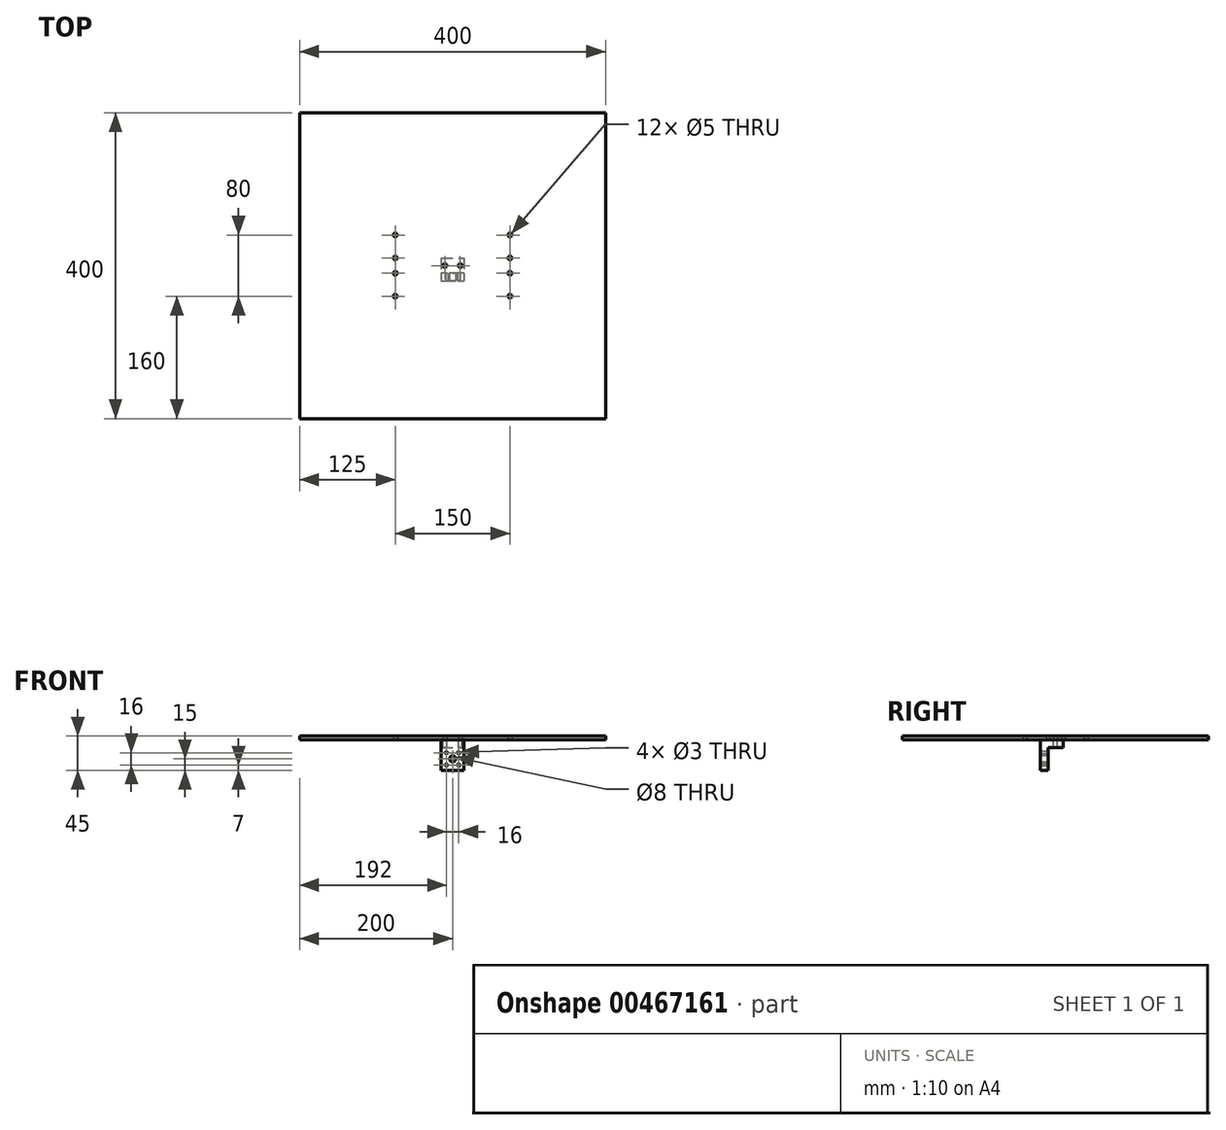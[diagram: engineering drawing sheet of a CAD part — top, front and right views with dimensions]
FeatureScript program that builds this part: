
annotation { "Feature Type Name" : "Feature", "Feature Type Description" : "" }
export const myFeature = defineFeature(function(context is Context, id is Id, definition is map)
    precondition{}
    {
        {
            var Q0;
            Q0=qCreatedBy(makeId("Top.planeOp"),FACE);
            var sketch = newSketch(context, id + "F0", { "sketchPlane" : qUnion([Q0])});
            skLineSegment(sketch, "E0.bottom", {"start": v(-200, 200) * mm, "end": v(200, 200) * mm});
            skLineSegment(sketch, "E0.top", {"start": v(-200, -200) * mm, "end": v(200, -200) * mm});
            skLineSegment(sketch, "E0.left", {"start": v(-200, 200) * mm, "end": v(-200, -200) * mm});
            skLineSegment(sketch, "E0.right", {"start": v(200, 200) * mm, "end": v(200, -200) * mm});
            skPoint(sketch, "E0.middle", {"position": v(0, 0) * mm});
            skPoint(sketch, "E1", {"position": v(-75, -10) * mm});
            skPoint(sketch, "E2", {"position": v(-75, -40) * mm});
            skPoint(sketch, "E3.0.1.0", {"position": v(-75, 40) * mm});
            skPoint(sketch, "E3.0.1.1", {"position": v(-75, 10) * mm});
            skPoint(sketch, "E3.1.0.0", {"position": v(75, -10) * mm});
            skPoint(sketch, "E3.1.0.1", {"position": v(75, -40) * mm});
            skPoint(sketch, "E3.1.1.0", {"position": v(75, 40) * mm});
            skPoint(sketch, "E3.1.1.1", {"position": v(75, 10) * mm});
            skLineSegment(sketch, "E3.direction1", {"start": v(-75, -40) * mm, "end": v(75, -40) * mm, "construction": true});
            skLineSegment(sketch, "E3.direction2", {"start": v(-75, -40) * mm, "end": v(-75, 10) * mm, "construction": true});
            skSolve(sketch);
        }
        {
            var Q0;
            Q0 = qSketchRegion(id + "F0", true);
            extrude(context, id + "F1", {"entities" : qUnion([Q0]), "depth" : 5 * mm});
        }
        {
            var Q0;
            Q0=makeQuery(id+"F0.imprint","IMPRINT",FACE,{"disambiguationData":[TD([[makeQuery(id+"F0.imprint","IMPRINT",EDGE,{"derivedFrom":sQuery(id+"F0.wireOp",EDGE,"E0.bottom")}),-1.0]])]});
            var sketch = newSketch(context, id + "F2", { "sketchPlane" : qUnion([Q0])});
            skPoint(sketch, "E4.middle", {"position": v(0, 0) * mm});
            skPoint(sketch, "E5", {"position": v(-10, 0) * mm});
            skPoint(sketch, "E6", {"position": v(10, 0) * mm});
            skSolve(sketch);
        }
        {
            var Q0;
            Q0=sQuery(id+"F0.wireOp",VERTEX,"E2");
            var Q1;
            Q1=sQuery(id+"F0.wireOp",VERTEX,"E1");
            var Q2;
            Q2=sQuery(id+"F0.wireOp",VERTEX,"E3.0.1.1");
            var Q3;
            Q3=sQuery(id+"F0.wireOp",VERTEX,"E3.0.1.0");
            var Q4;
            Q4=sQuery(id+"F0.wireOp",VERTEX,"E3.1.0.1");
            var Q5;
            Q5=sQuery(id+"F0.wireOp",VERTEX,"E3.1.0.0");
            var Q6;
            Q6=sQuery(id+"F0.wireOp",VERTEX,"E3.1.1.1");
            var Q7;
            Q7=sQuery(id+"F0.wireOp",VERTEX,"E3.1.1.0");
            var Q8;
            Q8=sQuery(id+"F2.wireOp",VERTEX,"E5");
            var Q9;
            Q9=sQuery(id+"F2.wireOp",VERTEX,"E6");
            var Q10;
            Q10=makeQuery(id+"F1.opExtrude","SWEPT_BODY",BODY,{"disambiguationData":[OSD([sQuery(id+"F0.wireOp",EDGE,"E0.bottom"),sQuery(id+"F0.wireOp",EDGE,"E0.top"),sQuery(id+"F0.wireOp",EDGE,"E0.left"),sQuery(id+"F0.wireOp",EDGE,"E0.right")])]});
            hole(context, id + "F3", {"style" : HoleStyle.SIMPLE, "endStyle" : HoleEndStyle.THROUGH, "oppositeDirection" : true, "holeDiameter" : 5 * mm, "isTappedThrough" : true, "tappedDepth" : 12 * mm, "tapClearance" : 3, "locations" : qUnion([Q0, Q1, Q2, Q3, Q4, Q5, Q6, Q7, Q8, Q9]), "scope" : qUnion([Q10])});
        }
        {
            var Q0;
            Q0=makeQuery(id+"F0.imprint","IMPRINT",FACE,{"disambiguationData":[TD([[makeQuery(id+"F0.imprint","IMPRINT",EDGE,{"derivedFrom":sQuery(id+"F0.wireOp",EDGE,"E0.bottom")}),-1.0]])]});
            var sketch = newSketch(context, id + "F4", { "sketchPlane" : qUnion([Q0])});
            skLineSegment(sketch, "E7.bottom", {"start": v(-15, 10) * mm, "end": v(15, 10) * mm});
            skLineSegment(sketch, "E7.top", {"start": v(-15, -20) * mm, "end": v(15, -20) * mm});
            skLineSegment(sketch, "E7.left", {"start": v(-15, 10) * mm, "end": v(-15, -20) * mm});
            skLineSegment(sketch, "E7.right", {"start": v(15, 10) * mm, "end": v(15, -20) * mm});
            skPoint(sketch, "E7.middle", {"position": v(0, 0) * mm});
            skCircle(sketch, "E8", {"center": v(-10, 0) * mm, "radius": 2.5 * mm});
            skCircle(sketch, "E9", {"center": v(10, 0) * mm, "radius": 2.5 * mm});
            skSolve(sketch);
        }
        {
            var Q0;
            Q0 = qSketchRegion(id + "F4", true);
            extrude(context, id + "F5", {"entities" : qUnion([Q0]), "oppositeDirection" : true, "depth" : 10 * mm});
        }
        {
            var Q0;
            Q0=makeQuery(id+"F5.opExtrude","CAP_FACE",FACE,{"disambiguationData":[OSD([sQuery(id+"F4.wireOp",EDGE,"E7.bottom"),sQuery(id+"F4.wireOp",EDGE,"E7.top"),sQuery(id+"F4.wireOp",EDGE,"E7.left"),sQuery(id+"F4.wireOp",EDGE,"E7.right")])],"isStart":false});
            var sketch = newSketch(context, id + "F6", { "sketchPlane" : qUnion([Q0])});
            skLineSegment(sketch, "E10.bottom", {"start": v(15, 10) * mm, "end": v(-15, 10) * mm});
            skLineSegment(sketch, "E10.top", {"start": v(15, 20) * mm, "end": v(-15, 20) * mm});
            skLineSegment(sketch, "E10.left", {"start": v(15, 10) * mm, "end": v(15, 20) * mm});
            skLineSegment(sketch, "E10.right", {"start": v(-15, 10) * mm, "end": v(-15, 20) * mm});
            skSolve(sketch);
        }
        {
            var Q0;
            Q0 = qSketchRegion(id + "F6", true);
            extrude(context, id + "F7", {"entities" : qUnion([Q0]), "operationType" : NewBodyOperationType.ADD, "depth" : 30 * mm});
        }
        {
            var Q0;
            Q0=makeQuery(id+"F7.boolean.opBoolean","MERGE",FACE,{"derivedFrom":[makeQuery(id+"F5.opExtrude","SWEPT_FACE",FACE,{"disambiguationData":[OSD([sQuery(id+"F4.wireOp",EDGE,"E7.top")])]}),makeQuery(id+"F7.opExtrude","SWEPT_FACE",FACE,{"disambiguationData":[OSD([sQuery(id+"F6.wireOp",EDGE,"E10.top")])]})]});
            var sketch = newSketch(context, id + "F8", { "sketchPlane" : qUnion([Q0])});
            skPoint(sketch, "E11", {"position": v(0, -25) * mm});
            skPoint(sketch, "E12", {"position": v(-8, -17) * mm});
            skLineSegment(sketch, "E13", {"start": v(-8, -17) * mm, "end": v(0, -17) * mm, "construction": true});
            skLineSegment(sketch, "E14", {"start": v(-8, -17) * mm, "end": v(-8, -25) * mm, "construction": true});
            skLineSegment(sketch, "E15", {"start": v(-8, -25) * mm, "end": v(0, -25) * mm, "construction": true});
            skPoint(sketch, "E16.0.1.0", {"position": v(-8, -33) * mm});
            skPoint(sketch, "E16.1.0.0", {"position": v(8, -17) * mm});
            skPoint(sketch, "E16.1.1.0", {"position": v(8, -33) * mm});
            skLineSegment(sketch, "E16.direction1", {"start": v(-8, -17) * mm, "end": v(8, -17) * mm, "construction": true});
            skLineSegment(sketch, "E16.direction2", {"start": v(-8, -17) * mm, "end": v(-8, -33) * mm, "construction": true});
            skCircle(sketch, "E17", {"center": v(0, -25) * mm, "radius": 15 * mm});
            skSolve(sketch);
        }
        {
            var Q0;
            Q0=sQuery(id+"F8.wireOp",VERTEX,"E12");
            var Q1;
            Q1=sQuery(id+"F8.wireOp",VERTEX,"E16.0.1.0");
            var Q2;
            Q2=sQuery(id+"F8.wireOp",VERTEX,"E16.1.0.0");
            var Q3;
            Q3=sQuery(id+"F8.wireOp",VERTEX,"E16.1.1.0");
            var Q4;
            Q4=makeQuery(id+"F5.opExtrude","SWEPT_BODY",BODY,{"disambiguationData":[OSD([sQuery(id+"F4.wireOp",EDGE,"E7.bottom"),sQuery(id+"F4.wireOp",EDGE,"E7.top"),sQuery(id+"F4.wireOp",EDGE,"E7.left"),sQuery(id+"F4.wireOp",EDGE,"E7.right")])]});
            hole(context, id + "F9", {"style" : HoleStyle.SIMPLE, "endStyle" : HoleEndStyle.THROUGH, "holeDiameter" : 3 * mm, "isTappedThrough" : true, "tappedDepth" : 12 * mm, "tapClearance" : 3, "locations" : qUnion([Q0, Q1, Q2, Q3]), "scope" : qUnion([Q4])});
        }
        {
            var Q0;
            Q0=sQuery(id+"F8.wireOp",VERTEX,"E11");
            var Q1;
            Q1=makeQuery(id+"F5.opExtrude","SWEPT_BODY",BODY,{"disambiguationData":[OSD([sQuery(id+"F4.wireOp",EDGE,"E7.bottom"),sQuery(id+"F4.wireOp",EDGE,"E7.top"),sQuery(id+"F4.wireOp",EDGE,"E7.left"),sQuery(id+"F4.wireOp",EDGE,"E7.right")])]});
            hole(context, id + "F10", {"style" : HoleStyle.SIMPLE, "endStyle" : HoleEndStyle.THROUGH, "holeDiameter" : 8 * mm, "isTappedThrough" : true, "tappedDepth" : 12 * mm, "tapClearance" : 3, "locations" : qUnion([Q0]), "scope" : qUnion([Q1])});
        }
    });
